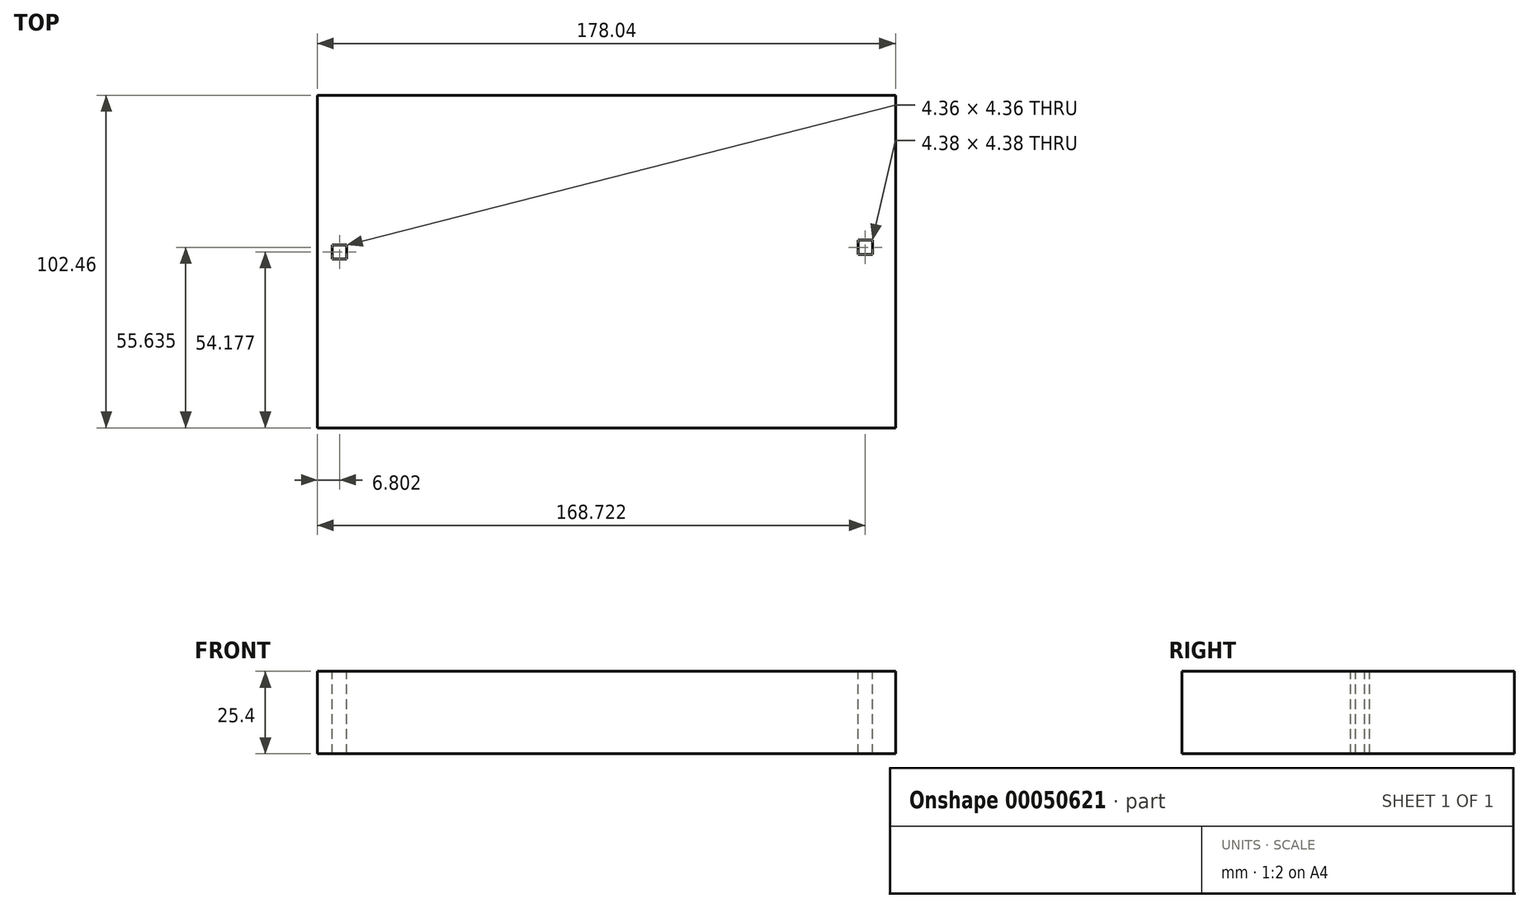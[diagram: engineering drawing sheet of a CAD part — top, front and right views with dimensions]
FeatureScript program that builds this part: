
annotation { "Feature Type Name" : "Feature", "Feature Type Description" : "" }
export const myFeature = defineFeature(function(context is Context, id is Id, definition is map)
    precondition{}
    {
        {
            var Q0;
            Q0=qCreatedBy(makeId("Top.planeOp"),FACE);
            var sketch = newSketch(context, id + "F0", { "sketchPlane" : qUnion([Q0])});
            skLineSegment(sketch, "E0.bottom", {"start": v(-37.23, 61.4) * mm, "end": v(140.8, 61.4) * mm});
            skLineSegment(sketch, "E0.top", {"start": v(-37.23, -41.06) * mm, "end": v(140.8, -41.06) * mm});
            skLineSegment(sketch, "E0.left", {"start": v(-37.23, 61.4) * mm, "end": v(-37.23, -41.06) * mm});
            skLineSegment(sketch, "E0.right", {"start": v(140.8, 61.4) * mm, "end": v(140.8, -41.06) * mm});
            skSolve(sketch);
        }
        {
            var Q0;
            Q0 = qSketchRegion(id + "F0", true);
            extrude(context, id + "F1", {"entities" : qUnion([Q0]), "depth" : 25.4 * mm});
        }
        {
            var Q0;
            Q0=makeQuery(id+"F1.opExtrude","CAP_FACE",FACE,{"disambiguationData":[OSD([sQuery(id+"F0.wireOp",EDGE,"E0.bottom"),sQuery(id+"F0.wireOp",EDGE,"E0.top"),sQuery(id+"F0.wireOp",EDGE,"E0.left"),sQuery(id+"F0.wireOp",EDGE,"E0.right")])],"isStart":false});
            var sketch = newSketch(context, id + "F2", { "sketchPlane" : qUnion([Q0])});
            skLineSegment(sketch, "E1.bottom", {"start": v(-32.6, 10.94) * mm, "end": v(-28.25, 10.94) * mm});
            skLineSegment(sketch, "E1.top", {"start": v(-32.6, 15.3) * mm, "end": v(-28.25, 15.3) * mm});
            skLineSegment(sketch, "E1.left", {"start": v(-32.6, 10.94) * mm, "end": v(-32.6, 15.3) * mm});
            skLineSegment(sketch, "E1.right", {"start": v(-28.25, 10.94) * mm, "end": v(-28.25, 15.3) * mm});
            skSolve(sketch);
        }
        {
            var Q0;
            Q0=makeQuery(id+"F2.imprint","IMPRINT",FACE,{"disambiguationData":[TD([[makeQuery(id+"F2.imprint","IMPRINT",EDGE,{"derivedFrom":sQuery(id+"F2.wireOp",EDGE,"E1.bottom")}),-1.0]])]});
            var sketch = newSketch(context, id + "F3", { "sketchPlane" : qUnion([Q0])});
            skLineSegment(sketch, "E2.bottom", {"start": v(133.68, 12.38) * mm, "end": v(129.3, 12.38) * mm});
            skLineSegment(sketch, "E2.top", {"start": v(133.68, 16.76) * mm, "end": v(129.3, 16.76) * mm});
            skLineSegment(sketch, "E2.left", {"start": v(133.68, 12.38) * mm, "end": v(133.68, 16.76) * mm});
            skLineSegment(sketch, "E2.right", {"start": v(129.3, 12.38) * mm, "end": v(129.3, 16.76) * mm});
            skSolve(sketch);
        }
        {
            var Q0;
            Q0=makeQuery(id+"F2.imprint","IMPRINT",FACE,{"disambiguationData":[TD([[makeQuery(id+"F2.imprint","IMPRINT",EDGE,{"derivedFrom":sQuery(id+"F2.wireOp",EDGE,"E1.bottom")}),1.0]])]});
            extrude(context, id + "F4", {"entities" : qUnion([Q0]), "operationType" : NewBodyOperationType.REMOVE, "oppositeDirection" : true, "depth" : 25.4 * mm});
        }
        {
            var Q0;
            Q0=makeQuery(id+"F3.imprint","IMPRINT",FACE,{"disambiguationData":[TD([[makeQuery(id+"F3.imprint","IMPRINT",EDGE,{"derivedFrom":sQuery(id+"F3.wireOp",EDGE,"E2.bottom")}),-1.0]])]});
            extrude(context, id + "F5", {"entities" : qUnion([Q0]), "operationType" : NewBodyOperationType.REMOVE, "oppositeDirection" : true, "depth" : 25.4 * mm});
        }
    });
